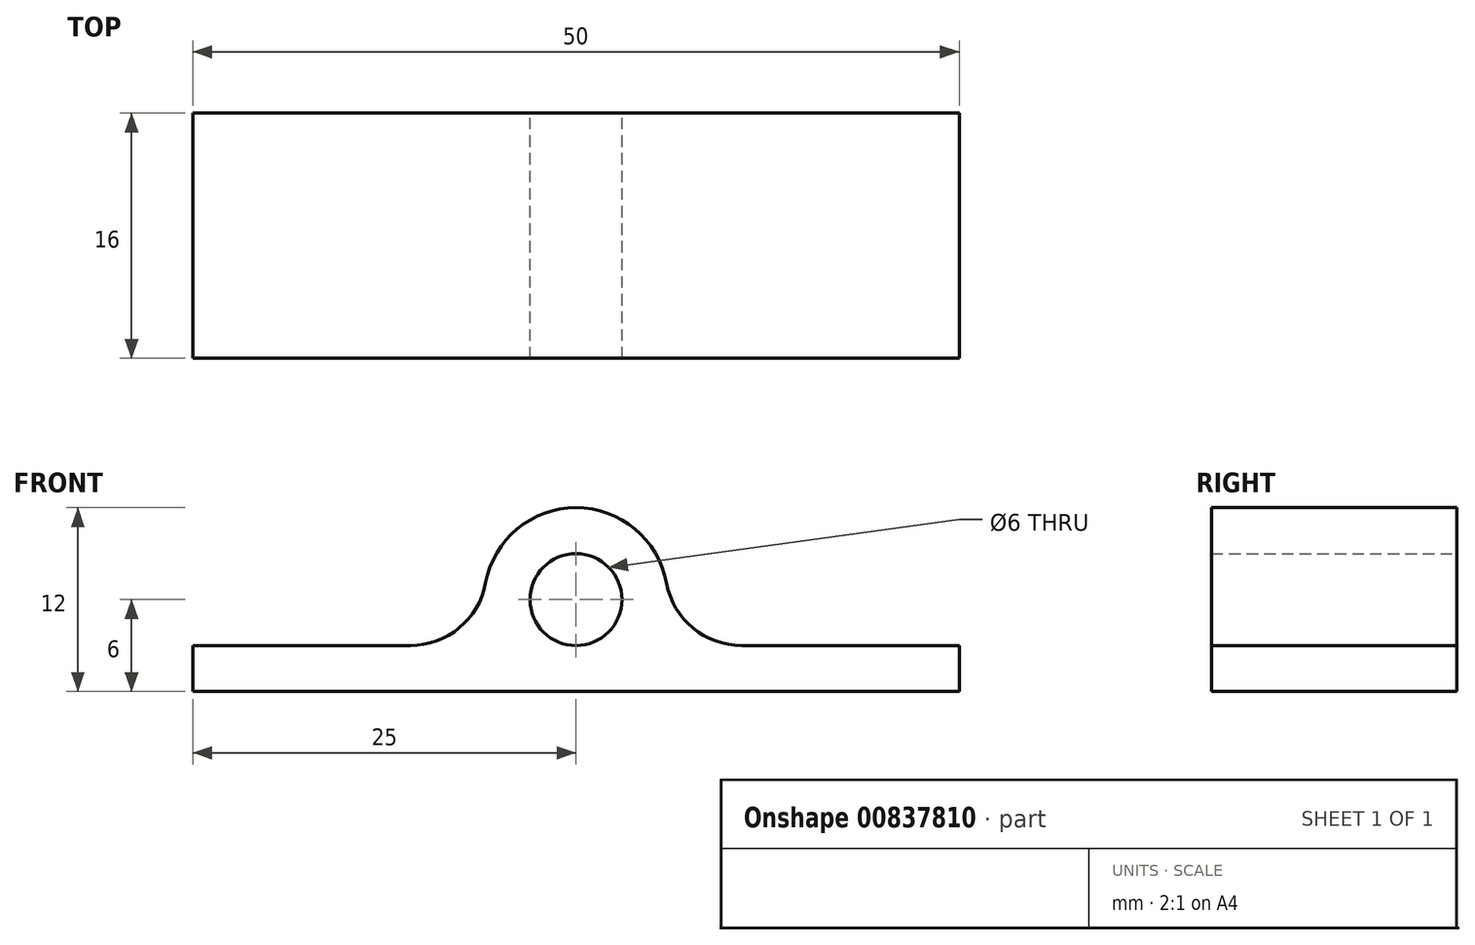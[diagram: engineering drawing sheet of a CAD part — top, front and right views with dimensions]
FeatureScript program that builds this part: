
annotation { "Feature Type Name" : "Feature", "Feature Type Description" : "" }
export const myFeature = defineFeature(function(context is Context, id is Id, definition is map)
    precondition{}
    {
        {
            var Q0;
            Q0=qCreatedBy(makeId("Top.planeOp"),FACE);
            var sketch = newSketch(context, id + "F0", { "sketchPlane" : qUnion([Q0])});
            skLineSegment(sketch, "E0.bottom", {"start": v(-25, 8) * mm, "end": v(25, 8) * mm});
            skLineSegment(sketch, "E0.top", {"start": v(-25, -8) * mm, "end": v(25, -8) * mm});
            skLineSegment(sketch, "E0.left", {"start": v(-25, 8) * mm, "end": v(-25, -8) * mm});
            skLineSegment(sketch, "E0.right", {"start": v(25, 8) * mm, "end": v(25, -8) * mm});
            skPoint(sketch, "E1", {"position": v(0, 8) * mm});
            skPoint(sketch, "E2", {"position": v(-25, 0) * mm});
            skSolve(sketch);
        }
        {
            var Q0;
            Q0=makeQuery(id+"F0.imprint","IMPRINT",FACE,{"disambiguationData":[TD([[makeQuery(id+"F0.imprint","IMPRINT",EDGE,{"derivedFrom":sQuery(id+"F0.wireOp",EDGE,"E0.bottom")}),-1.0]])]});
            extrude(context, id + "F1", {"entities" : qUnion([Q0]), "depth" : 3 * mm, "offsetDistance" : 25 * mm});
        }
        {
            var Q0;
            Q0=qCreatedBy(makeId("Front.planeOp"),FACE);
            var sketch = newSketch(context, id + "F2", { "sketchPlane" : qUnion([Q0])});
            skCircle(sketch, "E3", {"center": v(0, 6) * mm, "radius": 3 * mm});
            skCircle(sketch, "E4", {"center": v(0, 6) * mm, "radius": 6 * mm});
            skSolve(sketch);
        }
        {
            var Q0;
            Q0=makeQuery(id+"F2.imprint","IMPRINT",FACE,{"disambiguationData":[TD([[makeQuery(id+"F2.imprint","IMPRINT",EDGE,{"derivedFrom":sQuery(id+"F2.wireOp",EDGE,"E3")}),-1.0]])]});
            extrude(context, id + "F3", {"entities" : qUnion([Q0]), "operationType" : NewBodyOperationType.ADD, "endBound" : BoundingType.SYMMETRIC, "depth" : 16 * mm, "offsetDistance" : 25 * mm});
        }
        {
            var Q0;
            Q0=makeQuery(id+"F3.boolean.opBoolean","INTERSECT",EDGE,{"disambiguationData":[OD(1.0)],"derivedFrom":[makeQuery(id+"F1.opExtrude","CAP_FACE",FACE,{"disambiguationData":[OSD([sQuery(id+"F0.wireOp",EDGE,"E0.bottom"),sQuery(id+"F0.wireOp",EDGE,"E0.top"),sQuery(id+"F0.wireOp",EDGE,"E0.left"),sQuery(id+"F0.wireOp",EDGE,"E0.right")])],"isStart":false}),makeQuery(id+"F3.opExtrude","SWEPT_FACE",FACE,{"disambiguationData":[OSD([sQuery(id+"F2.wireOp",EDGE,"E4")])]})]});
            var Q1;
            Q1=makeQuery(id+"F3.boolean.opBoolean","INTERSECT",EDGE,{"disambiguationData":[OD(0.0)],"derivedFrom":[makeQuery(id+"F1.opExtrude","CAP_FACE",FACE,{"disambiguationData":[OSD([sQuery(id+"F0.wireOp",EDGE,"E0.bottom"),sQuery(id+"F0.wireOp",EDGE,"E0.top"),sQuery(id+"F0.wireOp",EDGE,"E0.left"),sQuery(id+"F0.wireOp",EDGE,"E0.right")])],"isStart":false}),makeQuery(id+"F3.opExtrude","SWEPT_FACE",FACE,{"disambiguationData":[OSD([sQuery(id+"F2.wireOp",EDGE,"E4")])]})]});
            fillet(context, id + "F4", {"entities" : qUnion([Q0, Q1]), "radius" : 5 * mm, "tangentPropagation" : true, "allowEdgeOverflow" : false});
        }
    });
